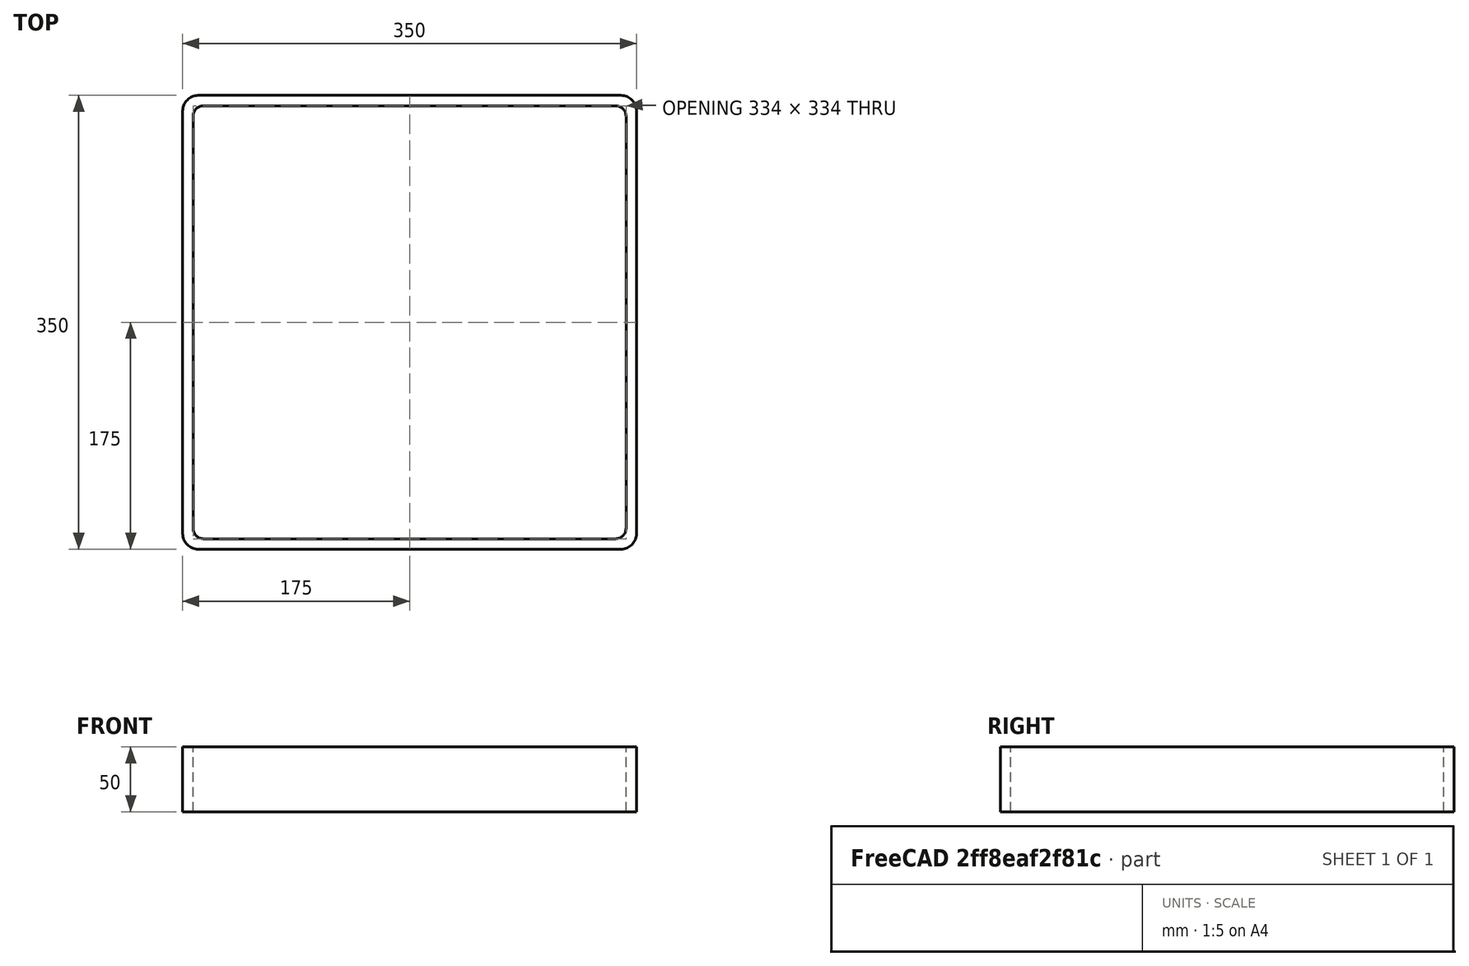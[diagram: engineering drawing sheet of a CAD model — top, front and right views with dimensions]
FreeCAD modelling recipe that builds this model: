
FCSTD DOCUMENT  (FreeCAD 0.15R4671 (Git))
Label: Square hollow section 350x350x8 EN10219 S235JRH
License: All rights reserved
LicenseURL: http://en.wikipedia.org/wiki/All_rights_reserved
objects: Sketcher::SketchObject×1, Part::Extrusion×1
note: 2 computed .brp shape members not serialized (recipe doc carries the construction recipe); baked Part::Feature solids carry a one-line shape summary decoded from their .brp

FEATURE [Sketcher::SketchObject] Sketch
  sketch-geometry (16):
    g0: LineSegment StartX=-159 StartY=167 StartZ=0 EndX=159 EndY=167 EndZ=0
    g1: LineSegment StartX=167 StartY=159 StartZ=0 EndX=167 EndY=-159 EndZ=0
    g2: LineSegment StartX=159 StartY=-167 StartZ=0 EndX=-159 EndY=-167 EndZ=0
    g3: LineSegment StartX=-167 StartY=-159 StartZ=0 EndX=-167 EndY=159 EndZ=0
    g4: LineSegment StartX=-163 StartY=175 StartZ=0 EndX=163 EndY=175 EndZ=0
    g5: LineSegment StartX=175 StartY=163 StartZ=0 EndX=175 EndY=-163 EndZ=0
    g6: LineSegment StartX=163 StartY=-175 StartZ=0 EndX=-163 EndY=-175 EndZ=0
    g7: LineSegment StartX=-175 StartY=-163 StartZ=0 EndX=-175 EndY=163 EndZ=0
    g8: ArcOfCircle CenterX=-159 CenterY=159 CenterZ=0 NormalX=0 NormalY=0 NormalZ=1 Radius=8 StartAngle=1.5708 EndAngle=3.14159
    g9: ArcOfCircle CenterX=159 CenterY=159 CenterZ=0 NormalX=0 NormalY=0 NormalZ=1 Radius=8 StartAngle=0 EndAngle=1.5708
    g10: ArcOfCircle CenterX=159 CenterY=-159 CenterZ=0 NormalX=0 NormalY=0 NormalZ=1 Radius=8 StartAngle=4.71239 EndAngle=6.28319
    g11: ArcOfCircle CenterX=-159 CenterY=-159 CenterZ=0 NormalX=0 NormalY=0 NormalZ=1 Radius=8 StartAngle=3.14159 EndAngle=4.71239
    g12: ArcOfCircle CenterX=163 CenterY=163 CenterZ=0 NormalX=0 NormalY=0 NormalZ=1 Radius=12 StartAngle=0 EndAngle=1.5708
    g13: ArcOfCircle CenterX=163 CenterY=-163 CenterZ=0 NormalX=0 NormalY=0 NormalZ=1 Radius=12 StartAngle=4.71239 EndAngle=6.28319
    g14: ArcOfCircle CenterX=-163 CenterY=-163 CenterZ=0 NormalX=0 NormalY=0 NormalZ=1 Radius=12 StartAngle=3.14159 EndAngle=4.71239
    g15: ArcOfCircle CenterX=-163 CenterY=163 CenterZ=0 NormalX=0 NormalY=0 NormalZ=1 Radius=12 StartAngle=1.5708 EndAngle=3.14159
  constraints (36):
    c: Horizontal(g2)
    c: Vertical(g3)
    c: Horizontal(g6)
    c: Vertical(g7)
    c: Tangent(g3,g8) = 1.5708
    c: Tangent(g0,g8) = 1.5708
    c: Tangent(g0,g9) = 1.5708
    c: Tangent(g1,g9) = 1.5708
    c: Tangent(g1,g10) = 1.5708
    c: Tangent(g2,g10) = 1.5708
    c: Tangent(g2,g11) = 1.5708
    c: Tangent(g3,g11) = 1.5708
    c: Tangent(g4,g12) = 1.5708
    c: Tangent(g5,g12) = 1.5708
    c: Tangent(g5,g13) = 1.5708
    c: Tangent(g6,g13) = 1.5708
    c: Tangent(g6,g14) = 1.5708
    c: Tangent(g7,g14) = 1.5708
    c: Tangent(g7,g15) = 1.5708
    c: Tangent(g4,g15) = 1.5708
    c: Equal(g9,g8)
    c: Equal(g9,g11)
    c: Equal(g9,g10)
    c: Equal(g12,g15)
    c: Equal(g12,g14)
    c: Equal(g12,g13)
    c: Symmetric(g4,g6,g-1)
    c: Symmetric(g7,g5,g-2)
    c: DistanceY(g4,g6) = -350
    c: DistanceX(g7,g5) = 350
    c: Symmetric(g3,g1,g-2)
    c: Symmetric(g0,g2,g-1)
    c: DistanceY(g0,g4) = 8
    c: DistanceX(g5,g1) = -8
    c: Radius(g9) = 8
    c: Radius(g12) = 12
FEATURE [Part::Extrusion] Extrude  label="Square hollow section 350x350x8 EN10219 S235JRH"
  Base = -> Sketch
  Dir = (0,0,50)
  Solid = true
